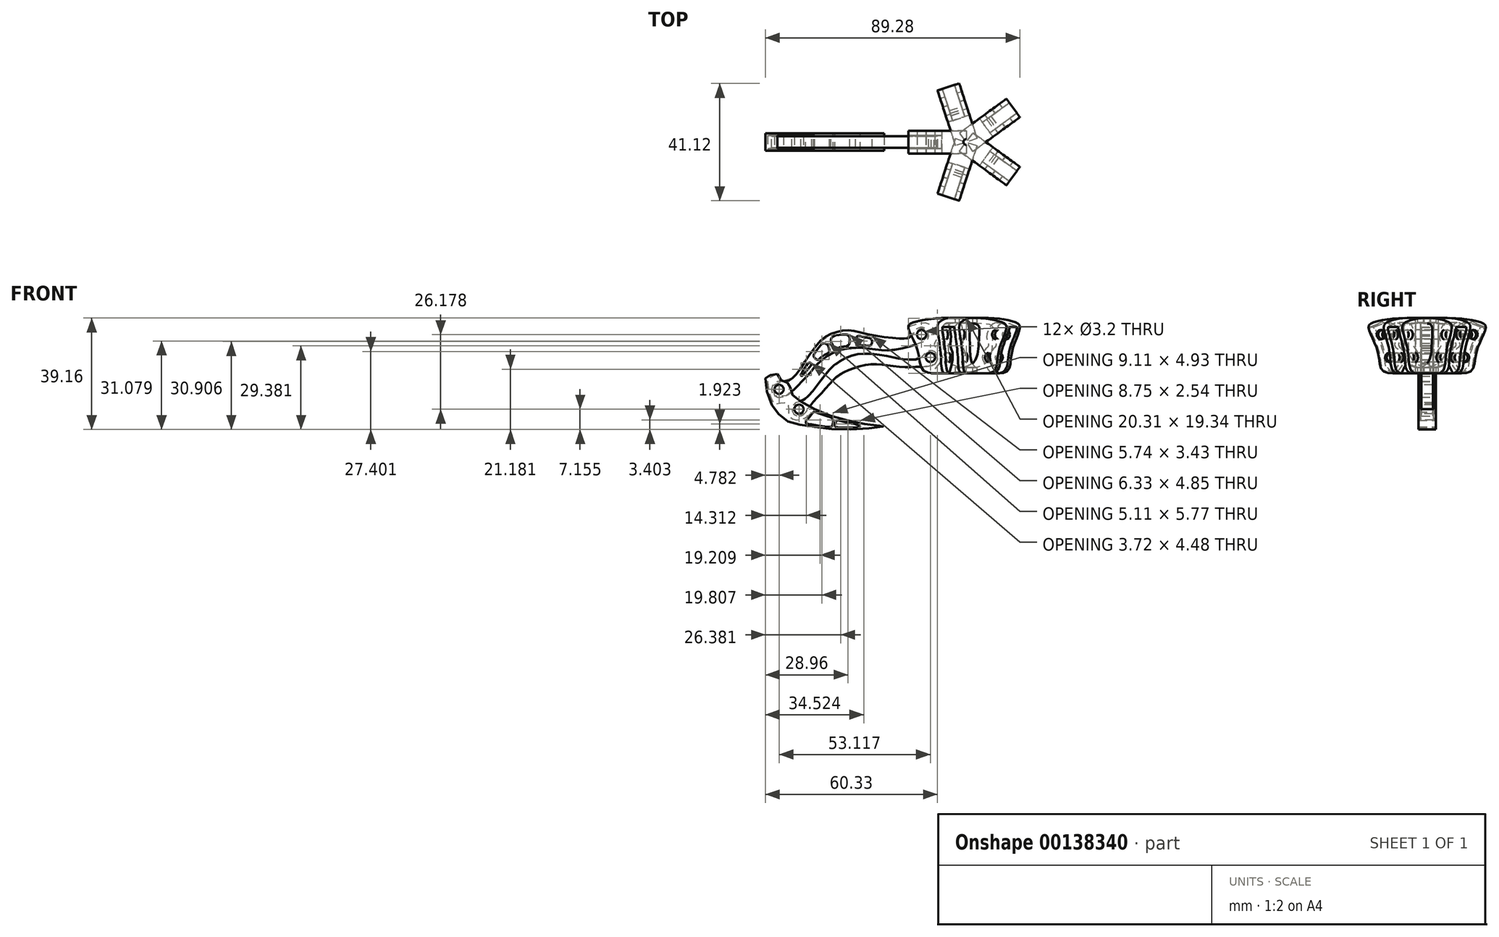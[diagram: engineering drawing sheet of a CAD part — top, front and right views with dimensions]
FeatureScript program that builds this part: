
annotation { "Feature Type Name" : "Feature", "Feature Type Description" : "" }
export const myFeature = defineFeature(function(context is Context, id is Id, definition is map)
    precondition{}
    {
        {
            var Q0;
            Q0=qCreatedBy(makeId("Front.planeOp"),FACE);
            var sketch = newSketch(context, id + "F0", { "sketchPlane" : qUnion([Q0])});
            skFitSpline(sketch, "E0", {"points": [v(-9.84, -8.79) * mm, v(-7.97, -7.5) * mm, v(-5.5, -5.04) * mm, v(-1.95, -1.3) * mm, v(1.5, 2.65) * mm, v(5.63, 5.7) * mm, v(10.96, 7.67) * mm, v(16.58, 7.97) * mm, v(22.3, 7.28) * mm, v(28.4, 7.28) * mm, v(35.6, 9.15) * mm, v(37.57, 9.94) * mm, v(38.56, 10.24) * mm, v(39.84, 11.12) * mm, v(40.03, 12.7) * mm, v(39.6, 14.2) * mm, v(38.24, 15.05) * mm, v(36.2, 14.77) * mm, v(35.2, 13.69) * mm, v(34.42, 12.4) * mm, v(33.33, 11.52) * mm, v(31.66, 11.22) * mm, v(29.1, 11.32) * mm, v(22.4, 12.01) * mm, v(16.18, 13.4) * mm, v(12.34, 14.08) * mm, v(8.99, 13.78) * mm, v(5.54, 12.7) * mm, v(2.28, 10.53) * mm, v(-2.25, 4.62) * mm, v(-6, -0.9) * mm, v(-7.97, -2.97) * mm, v(-9.45, -3.66) * mm, v(-11.22, -3.86) * mm, v(-12.6, -3.86) * mm, v(-14.28, -4.84) * mm, v(-14.97, -6.28) * mm, v(-14.77, -7.9) * mm, v(-13.73, -9) * mm, v(-12.3, -9.38) * mm, v(-9.84, -8.79) * mm]});
            skSolve(sketch);
        }
        {
            var Q0;
            Q0 = qSketchRegion(id + "F0", true);
            extrude(context, id + "F1", {"entities" : qUnion([Q0]), "endBound" : BoundingType.SYMMETRIC, "depth" : 4 * mm});
        }
        {
            var Q0;
            Q0=qCreatedBy(makeId("Front.planeOp"),FACE);
            var sketch = newSketch(context, id + "F2", { "sketchPlane" : qUnion([Q0])});
            skFitSpline(sketch, "E1", {"points": [v(-1.56, -12.53) * mm, v(2.58, -7.8) * mm, v(6.72, -3.27) * mm, v(9.58, -1) * mm, v(14.21, 0.97) * mm, v(20.52, 2.25) * mm, v(26.14, 1.76) * mm, v(32.54, 1.17) * mm, v(37.47, 1.37) * mm, v(42.03, 2.08) * mm, v(43.23, 4.05) * mm, v(42.95, 5.69) * mm, v(42, 6.66) * mm, v(40.58, 6.96) * mm, v(38.95, 6.3) * mm, v(37.77, 4.82) * mm, v(36.1, 3.93) * mm, v(33.82, 3.83) * mm, v(30.77, 4.03) * mm, v(26.83, 4.82) * mm, v(18.65, 5.9) * mm, v(12.53, 5.01) * mm, v(6.62, 1.56) * mm, v(2.88, -2.77) * mm, v(-1.76, -8.5) * mm, v(-4.6, -10.72) * mm, v(-6.53, -11.4) * mm, v(-7.68, -12.6) * mm, v(-7.7, -14.37) * mm, v(-6.29, -15.82) * mm, v(-3.84, -15.5) * mm, v(-1.56, -12.53) * mm]});
            skSolve(sketch);
        }
        {
            var Q0;
            Q0 = qSketchRegion(id + "F2", true);
            extrude(context, id + "F3", {"entities" : qUnion([Q0]), "endBound" : BoundingType.SYMMETRIC, "depth" : 4 * mm});
        }
        {
            var Q0;
            Q0=qCreatedBy(makeId("Front.planeOp"),FACE);
            var sketch = newSketch(context, id + "F4", { "sketchPlane" : qUnion([Q0])});
            skFitSpline(sketch, "E2", {"points": [v(-13, -1.2) * mm, v(-12.06, -3.03) * mm, v(-10.3, -3.8) * mm, v(-8.99, -4.78) * mm, v(-8.36, -6.13) * mm, v(-7.97, -8) * mm, v(-6.3, -9.77) * mm, v(1, -14.01) * mm, v(11.55, -17.46) * mm, v(22, -19.33) * mm, v(24.46, -19.53) * mm, v(20.22, -20.22) * mm, v(7.21, -20.62) * mm, v(-3.04, -19.33) * mm, v(-9.25, -17.95) * mm, v(-13, -14.7) * mm, v(-15.95, -9.87) * mm, v(-17.13, -2.77) * mm, v(-16.74, -2.28) * mm, v(-14.67, -1.3) * mm, v(-13, -1.2) * mm]});
            skSolve(sketch);
        }
        {
            var Q0;
            Q0 = qSketchRegion(id + "F4", true);
            extrude(context, id + "F5", {"entities" : qUnion([Q0]), "endBound" : BoundingType.SYMMETRIC, "oppositeDirection" : true, "depth" : 6 * mm});
        }
        {
            var Q0;
            Q0=qCreatedBy(makeId("Front.planeOp"),FACE);
            var sketch = newSketch(context, id + "F6", { "sketchPlane" : qUnion([Q0])});
            skFitSpline(sketch, "E3", {"points": [v(46.34, -1) * mm, v(42.7, -1) * mm, v(38.16, 0) * mm, v(36.68, 5.2) * mm, v(34.61, 11.02) * mm, v(33.13, 14.28) * mm, v(33.13, 15.85) * mm, v(34.42, 16.74) * mm, v(38.95, 17.83) * mm, v(48.02, 18.42) * mm, v(59.8, 16.6) * mm, v(59.6, 14.63) * mm, v(61.02, 7.55) * mm, v(60.23, 1.5) * mm, v(46.34, -1) * mm]});
            skSolve(sketch);
        }
        {
            var Q0;
            Q0=qCreatedBy(makeId("Front.planeOp"),FACE);
            var sketch = newSketch(context, id + "F7", { "sketchPlane" : qUnion([Q0])});
            skFitSpline(sketch, "E4", {"points": [v(-4.22, -1.79) * mm, v(-1.26, 1.66) * mm, v(-0.95, 2.25) * mm, v(-1.1, 2.57) * mm, v(-1.34, 2.73) * mm, v(-1.58, 2.73) * mm, v(-1.9, 2.69) * mm, v(-2.98, 1.52) * mm, v(-4.64, -1.36) * mm, v(-4.74, -1.68) * mm, v(-4.62, -1.9) * mm, v(-4.45, -1.96) * mm, v(-4.22, -1.79) * mm]});
            skSolve(sketch);
        }
        {
            var Q0;
            Q0=qCreatedBy(makeId("Front.planeOp"),FACE);
            var sketch = newSketch(context, id + "F8", { "sketchPlane" : qUnion([Q0])});
            skFitSpline(sketch, "E5", {"points": [v(1.67, 8.14) * mm, v(2.5, 9.14) * mm, v(3.2, 9.56) * mm, v(4.03, 9.42) * mm, v(4.78, 8.82) * mm, v(5.3, 7.12) * mm, v(5.19, 6.57) * mm, v(4.43, 5.89) * mm, v(3.11, 5.22) * mm, v(1.64, 3.97) * mm, v(1.11, 3.73) * mm, v(0.55, 3.94) * mm, v(0.13, 4.4) * mm, v(-0.17, 4.83) * mm, v(-0.2, 5.45) * mm, v(0.69, 6.87) * mm, v(1.67, 8.14) * mm]});
            skSolve(sketch);
        }
        {
            var Q0;
            Q0=qCreatedBy(makeId("Front.planeOp"),FACE);
            var sketch = newSketch(context, id + "F9", { "sketchPlane" : qUnion([Q0])});
            skFitSpline(sketch, "E6", {"points": [v(8.71, 12.52) * mm, v(10.55, 12.64) * mm, v(11.47, 12.55) * mm, v(12.17, 12.08) * mm, v(12.36, 11.39) * mm, v(12.42, 9.92) * mm, v(12.25, 9.2) * mm, v(11.72, 8.68) * mm, v(9.95, 8.41) * mm, v(8.45, 7.93) * mm, v(7.92, 7.75) * mm, v(7.2, 7.91) * mm, v(6.73, 8.47) * mm, v(5.9, 10.2) * mm, v(5.9, 11.02) * mm, v(6.45, 11.84) * mm, v(8.71, 12.52) * mm]});
            skSolve(sketch);
        }
        {
            var Q0;
            Q0=qCreatedBy(makeId("Front.planeOp"),FACE);
            var sketch = newSketch(context, id + "F10", { "sketchPlane" : qUnion([Q0])});
            skFitSpline(sketch, "E7", {"points": [v(17.77, 11.64) * mm, v(19.33, 11.4) * mm, v(20.03, 11.01) * mm, v(20.24, 10.3) * mm, v(20.2, 9.58) * mm, v(19.88, 8.94) * mm, v(19.4, 8.64) * mm, v(17.75, 8.82) * mm, v(16.1, 8.8) * mm, v(15.27, 8.8) * mm, v(14.73, 9.24) * mm, v(14.53, 10.07) * mm, v(14.55, 11.33) * mm, v(15.08, 11.95) * mm, v(16.13, 12.05) * mm, v(17.77, 11.64) * mm]});
            skSolve(sketch);
        }
        {
            var Q0;
            Q0 = qSketchRegion(id + "F7", true);
            var Q1;
            Q1 = qSketchRegion(id + "F8", true);
            var Q2;
            Q2 = qSketchRegion(id + "F9", true);
            var Q3;
            Q3 = qSketchRegion(id + "F10", true);
            extrude(context, id + "F11", {"entities" : qUnion([Q0, Q1, Q2, Q3]), "endBound" : BoundingType.SYMMETRIC, "depth" : 25 * mm});
        }
        {
            var Q0;
            Q0=makeQuery(id+"F11.opExtrude","SWEPT_BODY",BODY,{"disambiguationData":[OSD([sQuery(id+"F7.wireOp",EDGE,"E4")])]});
            var Q1;
            Q1=makeQuery(id+"F11.opExtrude","SWEPT_BODY",BODY,{"disambiguationData":[OSD([sQuery(id+"F8.wireOp",EDGE,"E5")])]});
            var Q2;
            Q2=makeQuery(id+"F11.opExtrude","SWEPT_BODY",BODY,{"disambiguationData":[OSD([sQuery(id+"F9.wireOp",EDGE,"E6")])]});
            var Q3;
            Q3=makeQuery(id+"F11.opExtrude","SWEPT_BODY",BODY,{"disambiguationData":[OSD([sQuery(id+"F10.wireOp",EDGE,"E7")])]});
            var Q4;
            Q4=makeQuery(id+"F1.opExtrude","SWEPT_BODY",BODY,{"disambiguationData":[OSD([sQuery(id+"F0.wireOp",EDGE,"E0")])]});
            booleanBodies(context, id + "F12", {"operationType" : BooleanOperationType.SUBTRACTION, "tools" : qUnion([Q0, Q1, Q2, Q3]), "targets" : qUnion([Q4])});
        }
        {
            var Q0;
            Q0=qCreatedBy(makeId("Front.planeOp"),FACE);
            var sketch = newSketch(context, id + "F13", { "sketchPlane" : qUnion([Q0])});
            skFitSpline(sketch, "E8", {"points": [v(-16.08, -2.67) * mm, v(-16.44, -3.93) * mm, v(-16.17, -6) * mm, v(-15.58, -8.67) * mm, v(-14.13, -11.6) * mm, v(-12.95, -11.65) * mm, v(-10.76, -11.26) * mm, v(-9.43, -11.45) * mm, v(-9.11, -12.4) * mm, v(-9.08, -14) * mm, v(-8.72, -16.04) * mm, v(-7.47, -17.02) * mm, v(-5.4, -17.37) * mm, v(-3, -16.47) * mm, v(-1.36, -15.21) * mm, v(0.91, -12.7) * mm, v(1.58, -11.53) * mm, v(-8.68, 1.32) * mm, v(-12.28, -0.87) * mm, v(-16.08, -2.67) * mm]});
            skSolve(sketch);
        }
        {
            var Q0;
            Q0=qCreatedBy(makeId("Front.planeOp"),FACE);
            var sketch = newSketch(context, id + "F14", { "sketchPlane" : qUnion([Q0])});
            skFitSpline(sketch, "E9", {"points": [v(-0.58, -14.86) * mm, v(-1.48, -16.08) * mm, v(-2.42, -17.05) * mm, v(-2.96, -17.88) * mm, v(-2.93, -18.5) * mm, v(-1.44, -18.86) * mm, v(1.85, -19.33) * mm, v(5.57, -19.8) * mm, v(6.16, -19.64) * mm, v(6.4, -18.97) * mm, v(6.63, -17.52) * mm, v(6.48, -16.98) * mm, v(5.42, -16.35) * mm, v(2.36, -15.33) * mm, v(0.64, -14.67) * mm, v(0, -14.59) * mm, v(-0.58, -14.86) * mm]});
            skSolve(sketch);
        }
        {
            var Q0;
            Q0=qCreatedBy(makeId("Front.planeOp"),FACE);
            var sketch = newSketch(context, id + "F15", { "sketchPlane" : qUnion([Q0])});
            skFitSpline(sketch, "E10", {"points": [v(7.42, -18.43) * mm, v(7.26, -19.2) * mm, v(7.34, -19.56) * mm, v(7.77, -19.87) * mm, v(11.9, -20.06) * mm, v(15.15, -19.98) * mm, v(16.16, -19.57) * mm, v(14.55, -18.9) * mm, v(11.4, -18.25) * mm, v(8.68, -17.55) * mm, v(7.85, -17.6) * mm, v(7.61, -17.8) * mm, v(7.42, -18.43) * mm]});
            skSolve(sketch);
        }
        {
            var Q0;
            Q0 = qSketchRegion(id + "F13", true);
            extrude(context, id + "F16", {"entities" : qUnion([Q0]), "endBound" : BoundingType.SYMMETRIC, "depth" : 4.5 * mm});
        }
        {
            var Q0;
            Q0 = qSketchRegion(id + "F14", true);
            var Q1;
            Q1 = qSketchRegion(id + "F15", true);
            extrude(context, id + "F17", {"entities" : qUnion([Q0, Q1]), "endBound" : BoundingType.SYMMETRIC, "depth" : 25 * mm});
        }
        {
            var Q0;
            Q0=makeQuery(id+"F16.opExtrude","SWEPT_BODY",BODY,{"disambiguationData":[OSD([sQuery(id+"F13.wireOp",EDGE,"E8")])]});
            var Q1;
            Q1=makeQuery(id+"F17.opExtrude","SWEPT_BODY",BODY,{"disambiguationData":[OSD([sQuery(id+"F14.wireOp",EDGE,"E9")])]});
            var Q2;
            Q2=makeQuery(id+"F17.opExtrude","SWEPT_BODY",BODY,{"disambiguationData":[OSD([sQuery(id+"F15.wireOp",EDGE,"E10")])]});
            var Q3;
            Q3=makeQuery(id+"F5.opExtrude","SWEPT_BODY",BODY,{"disambiguationData":[OSD([sQuery(id+"F4.wireOp",EDGE,"E2")])]});
            booleanBodies(context, id + "F18", {"operationType" : BooleanOperationType.SUBTRACTION, "tools" : qUnion([Q0, Q1, Q2]), "targets" : qUnion([Q3])});
        }
        {
            var Q0;
            Q0 = qSketchRegion(id + "F6", true);
            extrude(context, id + "F19", {"entities" : qUnion([Q0]), "endBound" : BoundingType.SYMMETRIC, "oppositeDirection" : true, "depth" : 8 * mm});
        }
        {
            var Q0;
            Q0=qCreatedBy(makeId("Front.planeOp"),FACE);
            var sketch = newSketch(context, id + "F20", { "sketchPlane" : qUnion([Q0])});
            skFitSpline(sketch, "E11", {"points": [v(32.4, 15.18) * mm, v(35.24, 16.12) * mm, v(37.84, 16.74) * mm, v(40.23, 16.32) * mm, v(42.3, 13.78) * mm, v(42.72, 10.67) * mm, v(41.99, 9.22) * mm, v(42.66, 7.97) * mm, v(44.32, 6.52) * mm, v(44.64, 4.23) * mm, v(43.7, 2.37) * mm, v(39.91, -2) * mm, v(35.09, -2.93) * mm, v(30.26, 13.78) * mm, v(32.4, 15.18) * mm]});
            skSolve(sketch);
        }
        {
            var Q0;
            Q0 = qSketchRegion(id + "F20", true);
            extrude(context, id + "F21", {"entities" : qUnion([Q0]), "endBound" : BoundingType.SYMMETRIC, "depth" : 4.5 * mm});
        }
        {
            var Q0;
            Q0=qCreatedBy(makeId("Front.planeOp"),FACE);
            var sketch = newSketch(context, id + "F22", { "sketchPlane" : qUnion([Q0])});
            skLineSegment(sketch, "E12.bottom", {"start": v(53.31, 22.4) * mm, "end": v(63.83, 22.4) * mm});
            skLineSegment(sketch, "E12.top", {"start": v(53.31, -8.27) * mm, "end": v(63.83, -8.27) * mm});
            skLineSegment(sketch, "E12.left", {"start": v(53.31, 22.4) * mm, "end": v(53.31, -8.27) * mm});
            skLineSegment(sketch, "E12.right", {"start": v(63.83, 22.4) * mm, "end": v(63.83, -8.27) * mm});
            skSolve(sketch);
        }
        {
            var Q0;
            Q0 = qSketchRegion(id + "F22", true);
            extrude(context, id + "F23", {"entities" : qUnion([Q0]), "endBound" : BoundingType.SYMMETRIC, "depth" : 25 * mm});
        }
        {
            var Q0;
            Q0=qCreatedBy(makeId("Front.planeOp"),FACE);
            var sketch = newSketch(context, id + "F24", { "sketchPlane" : qUnion([Q0])});
            skFitSpline(sketch, "E13", {"points": [v(55.73, 16.72) * mm, v(47.98, 16.46) * mm, v(45.36, 15.93) * mm, v(44.83, 15.2) * mm, v(44.68, 14.05) * mm, v(45, 10.22) * mm, v(45.57, 5.5) * mm, v(46.88, 3.3) * mm, v(48.4, 2.2) * mm, v(53.52, 1.06) * mm, v(55.94, 2.26) * mm, v(56.3, 2.42) * mm, v(56.52, 2.52) * mm, v(56.67, 3.1) * mm, v(56.67, 3.57) * mm, v(57.15, 15.25) * mm, v(57.15, 15.57) * mm, v(56.99, 15.83) * mm, v(56.83, 16.2) * mm, v(56.36, 16.51) * mm, v(55.73, 16.72) * mm]});
            skSolve(sketch);
        }
        {
            var Q0;
            Q0=makeQuery(id+"F24.imprint","IMPRINT",FACE,{"disambiguationData":[TD([[makeQuery(id+"F24.imprint","IMPRINT",EDGE,{"derivedFrom":sQuery(id+"F24.wireOp",EDGE,"E13")}),1.0]])]});
            extrude(context, id + "F25", {"entities" : qUnion([Q0]), "endBound" : BoundingType.SYMMETRIC, "depth" : 25 * mm});
        }
        {
            var Q0;
            Q0=makeQuery(id+"F21.opExtrude","SWEPT_BODY",BODY,{"disambiguationData":[OSD([sQuery(id+"F20.wireOp",EDGE,"E11")])]});
            var Q1;
            Q1=makeQuery(id+"F23.opExtrude","SWEPT_BODY",BODY,{"disambiguationData":[OSD([sQuery(id+"F22.wireOp",EDGE,"E12.bottom"),sQuery(id+"F22.wireOp",EDGE,"E12.top"),sQuery(id+"F22.wireOp",EDGE,"E12.left"),sQuery(id+"F22.wireOp",EDGE,"E12.right")])]});
            var Q2;
            Q2=makeQuery(id+"F25.opExtrude","SWEPT_BODY",BODY,{"disambiguationData":[OSD([sQuery(id+"F24.wireOp",EDGE,"E13")])]});
            var Q3;
            Q3=makeQuery(id+"F19.opExtrude","SWEPT_BODY",BODY,{"disambiguationData":[OSD([sQuery(id+"F6.wireOp",EDGE,"E3")])]});
            booleanBodies(context, id + "F26", {"operationType" : BooleanOperationType.SUBTRACTION, "tools" : qUnion([Q0, Q1, Q2]), "targets" : qUnion([Q3])});
        }
        {
            var Q0;
            Q0=qCreatedBy(makeId("Front.planeOp"),FACE);
            cPlane(context, id + "F27", {"entities" : qUnion([Q0]), "cplaneType" : CPlaneType.OFFSET, "offset" : 10 * mm, "width" : 150 * mm, "height" : 150 * mm});
        }
        {
            var Q0;
            Q0=qCreatedBy(id+"F27.planeOp",FACE);
            var sketch = newSketch(context, id + "F28", { "sketchPlane" : qUnion([Q0])});
            skLineSegment(sketch, "E14.bottom", {"start": v(-12.39, -6.62) * mm, "end": v(-5.37, -6.62) * mm});
            skLineSegment(sketch, "E14.top", {"start": v(-12.39, -13.58) * mm, "end": v(-5.37, -13.58) * mm});
            skLineSegment(sketch, "E14.left", {"start": v(-12.39, -6.62) * mm, "end": v(-12.39, -13.58) * mm});
            skLineSegment(sketch, "E14.right", {"start": v(-5.37, -6.62) * mm, "end": v(-5.37, -13.58) * mm});
            skSolve(sketch);
        }
        {
            var Q0;
            Q0=qCreatedBy(id+"F27.planeOp",FACE);
            var sketch = newSketch(context, id + "F29", { "sketchPlane" : qUnion([Q0])});
            skLineSegment(sketch, "E15.bottom", {"start": v(37.6, 12.6) * mm, "end": v(40.73, 12.6) * mm});
            skLineSegment(sketch, "E15.top", {"start": v(37.6, 4.59) * mm, "end": v(40.73, 4.59) * mm});
            skLineSegment(sketch, "E15.left", {"start": v(37.6, 12.6) * mm, "end": v(37.6, 4.59) * mm});
            skLineSegment(sketch, "E15.right", {"start": v(40.73, 12.6) * mm, "end": v(40.73, 4.59) * mm});
            skSolve(sketch);
        }
        {
            var Q0;
            Q0=sQuery(id+"F28.wireOp",VERTEX,"E14.left.start");
            var Q1;
            Q1=sQuery(id+"F28.wireOp",VERTEX,"E14.right.end");
            var Q2;
            Q2=makeQuery(id+"F1.opExtrude","SWEPT_BODY",BODY,{"disambiguationData":[OSD([sQuery(id+"F0.wireOp",EDGE,"E0")])]});
            var Q3;
            Q3=makeQuery(id+"F5.opExtrude","SWEPT_BODY",BODY,{"disambiguationData":[OSD([sQuery(id+"F4.wireOp",EDGE,"E2")])]});
            var Q4;
            Q4=makeQuery(id+"F3.opExtrude","SWEPT_BODY",BODY,{"disambiguationData":[OSD([sQuery(id+"F2.wireOp",EDGE,"E1")])]});
            hole(context, id + "F30", {"style" : HoleStyle.SIMPLE, "endStyle" : HoleEndStyle.BLIND, "holeDiameter" : 3.2 * mm, "holeDepth" : 30 * mm, "locations" : qUnion([Q0, Q1]), "scope" : qUnion([Q2, Q3, Q4])});
        }
        {
            var Q0;
            Q0=sQuery(id+"F29.wireOp",VERTEX,"E15.bottom.start");
            var Q1;
            Q1=sQuery(id+"F29.wireOp",VERTEX,"E15.right.end");
            var Q2;
            Q2=makeQuery(id+"F1.opExtrude","SWEPT_BODY",BODY,{"disambiguationData":[OSD([sQuery(id+"F0.wireOp",EDGE,"E0")])]});
            var Q3;
            Q3=makeQuery(id+"F3.opExtrude","SWEPT_BODY",BODY,{"disambiguationData":[OSD([sQuery(id+"F2.wireOp",EDGE,"E1")])]});
            var Q4;
            Q4=makeQuery(id+"F19.opExtrude","SWEPT_BODY",BODY,{"disambiguationData":[OSD([sQuery(id+"F6.wireOp",EDGE,"E3")])]});
            hole(context, id + "F31", {"style" : HoleStyle.SIMPLE, "endStyle" : HoleEndStyle.BLIND, "holeDiameter" : 3.2 * mm, "holeDepth" : 30 * mm, "startFromSketch" : true, "locations" : qUnion([Q0, Q1]), "scope" : qUnion([Q2, Q3, Q4])});
        }
        {
            var Q0;
            Q0=qCreatedBy(makeId("Front.planeOp"),FACE);
            var sketch = newSketch(context, id + "F32", { "sketchPlane" : qUnion([Q0])});
            skLineSegment(sketch, "E16", {"start": v(53.31, 21.77) * mm, "end": v(53.31, -3.82) * mm});
            skSolve(sketch);
        }
        {
            var Q0;
            Q0=makeQuery(id+"F19.opExtrude","SWEPT_BODY",BODY,{"disambiguationData":[OSD([sQuery(id+"F6.wireOp",EDGE,"E3")])]});
            var Q1;
            Q1=sQuery(id+"F32.wireOp",EDGE,"E16");
            transform(context, id + "F33", {"entities" : qUnion([Q0]), "transformType" : TransformType.ROTATION, "transformAxis" : qUnion([Q1]), "angle" : 72 * degree, "makeCopy" : true});
        }
        {
            var Q0;
            Q0=makeQuery(id+"F33.opPattern","COPY",BODY,{"derivedFrom":makeQuery(id+"F19.opExtrude","SWEPT_BODY",BODY,{"disambiguationData":[OSD([sQuery(id+"F6.wireOp",EDGE,"E3")])]}),"instanceName":"1"});
            var Q1;
            Q1=sQuery(id+"F32.wireOp",EDGE,"E16");
            transform(context, id + "F34", {"entities" : qUnion([Q0]), "transformType" : TransformType.ROTATION, "transformAxis" : qUnion([Q1]), "angle" : 72 * degree, "makeCopy" : true});
        }
        {
            var Q0;
            Q0=makeQuery(id+"F34.opPattern","COPY",BODY,{"derivedFrom":makeQuery(id+"F33.opPattern","COPY",BODY,{"derivedFrom":makeQuery(id+"F19.opExtrude","SWEPT_BODY",BODY,{"disambiguationData":[OSD([sQuery(id+"F6.wireOp",EDGE,"E3")])]}),"instanceName":"1"}),"instanceName":"1"});
            var Q1;
            Q1=sQuery(id+"F32.wireOp",EDGE,"E16");
            transform(context, id + "F35", {"entities" : qUnion([Q0]), "transformType" : TransformType.ROTATION, "transformAxis" : qUnion([Q1]), "angle" : 72 * degree, "makeCopy" : true});
        }
        {
            var Q0;
            Q0=makeQuery(id+"F35.opPattern","COPY",BODY,{"derivedFrom":makeQuery(id+"F34.opPattern","COPY",BODY,{"derivedFrom":makeQuery(id+"F33.opPattern","COPY",BODY,{"derivedFrom":makeQuery(id+"F19.opExtrude","SWEPT_BODY",BODY,{"disambiguationData":[OSD([sQuery(id+"F6.wireOp",EDGE,"E3")])]}),"instanceName":"1"}),"instanceName":"1"}),"instanceName":"1"});
            var Q1;
            Q1=sQuery(id+"F32.wireOp",EDGE,"E16");
            transform(context, id + "F36", {"entities" : qUnion([Q0]), "transformType" : TransformType.ROTATION, "transformAxis" : qUnion([Q1]), "angle" : 72 * degree, "makeCopy" : true});
        }
        {
            var Q0;
            Q0=qCreatedBy(makeId("Top.planeOp"),FACE);
            cPlane(context, id + "F37", {"entities" : qUnion([Q0]), "cplaneType" : CPlaneType.OFFSET, "offset" : 25 * mm, "width" : 150 * mm, "height" : 150 * mm});
        }
        {
            var Q0;
            Q0=qCreatedBy(id+"F37.planeOp",FACE);
            var sketch = newSketch(context, id + "F38", { "sketchPlane" : qUnion([Q0])});
            skLineSegment(sketch, "E17.bottom", {"start": v(0, 0) * mm, "end": v(53.31, 0) * mm});
            skLineSegment(sketch, "E17.top", {"start": v(0, -25.05) * mm, "end": v(53.31, -25.05) * mm});
            skLineSegment(sketch, "E17.left", {"start": v(0, 0) * mm, "end": v(0, -25.05) * mm});
            skLineSegment(sketch, "E17.right", {"start": v(53.31, 0) * mm, "end": v(53.31, -25.05) * mm});
            skSolve(sketch);
        }
        {
            var Q0;
            Q0=sQuery(id+"F38.wireOp",VERTEX,"E17.right.start");
            var Q1;
            Q1=makeQuery(id+"F19.opExtrude","SWEPT_BODY",BODY,{"disambiguationData":[OSD([sQuery(id+"F6.wireOp",EDGE,"E3")])]});
            hole(context, id + "F39", {"style" : HoleStyle.SIMPLE, "endStyle" : HoleEndStyle.BLIND, "holeDiameter" : 2 * mm, "holeDepth" : 30 * mm, "locations" : qUnion([Q0]), "scope" : qUnion([Q1])});
        }
    });
